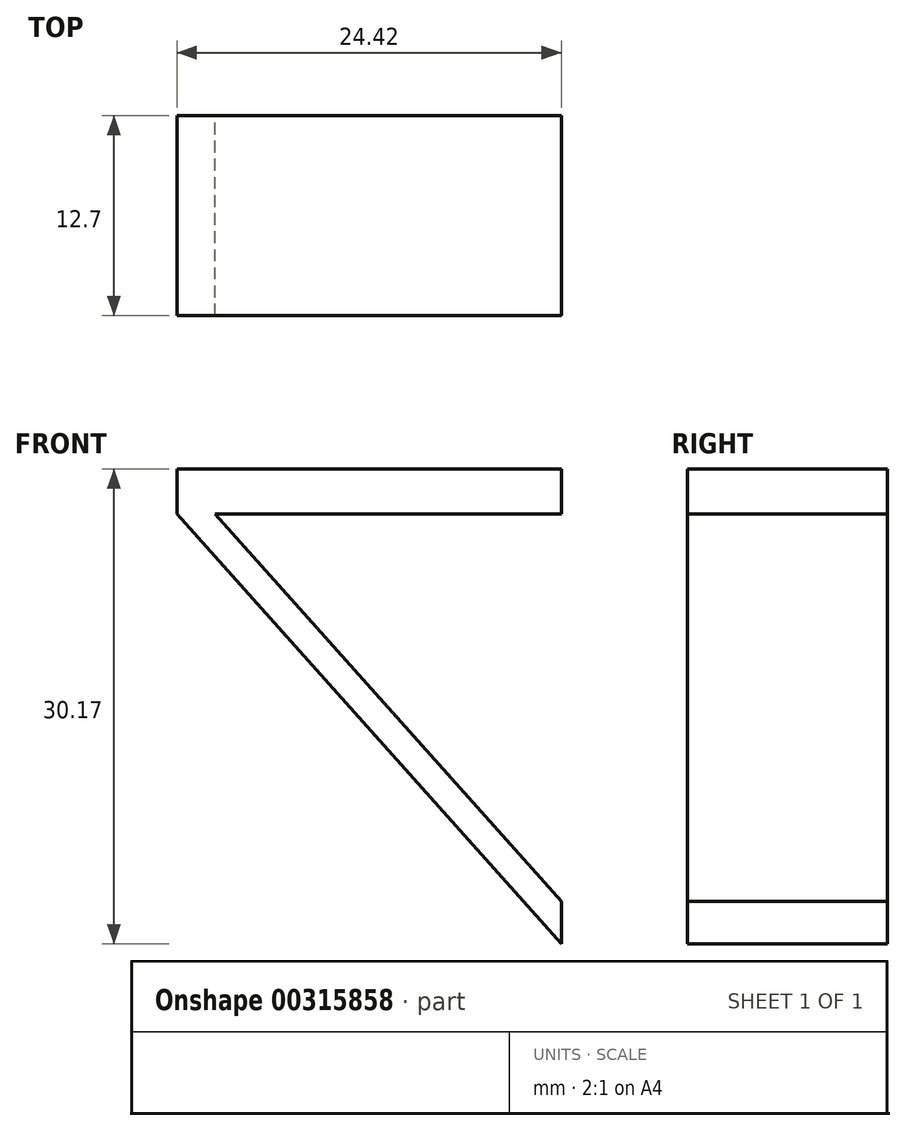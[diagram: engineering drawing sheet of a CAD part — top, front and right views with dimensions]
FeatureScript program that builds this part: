
annotation { "Feature Type Name" : "Feature", "Feature Type Description" : "" }
export const myFeature = defineFeature(function(context is Context, id is Id, definition is map)
    precondition{}
    {
        {
            var Q0;
            Q0=qCreatedBy(makeId("Front.planeOp"),FACE);
            var sketch = newSketch(context, id + "F0", { "sketchPlane" : qUnion([Q0])});
            skLineSegment(sketch, "E0", {"start": v(0, 0) * mm, "end": v(-21.99, 0) * mm});
            skLineSegment(sketch, "E1", {"start": v(-21.99, 0) * mm, "end": v(-21.99, 2.86) * mm});
            skLineSegment(sketch, "E2", {"start": v(0, 0) * mm, "end": v(0, 2.86) * mm});
            skLineSegment(sketch, "E3", {"start": v(0, 2.86) * mm, "end": v(0, 0) * mm});
            skLineSegment(sketch, "E4", {"start": v(-21.99, 2.86) * mm, "end": v(0, 2.86) * mm});
            skLineSegment(sketch, "E5", {"start": v(-21.99, 0) * mm, "end": v(0, -24.6) * mm});
            skLineSegment(sketch, "E6", {"start": v(0, -24.6) * mm, "end": v(0, -27.3) * mm});
            skLineSegment(sketch, "E7", {"start": v(0, -27.3) * mm, "end": v(-21.99, -2.72) * mm});
            skLineSegment(sketch, "E8", {"start": v(-21.99, -2.72) * mm, "end": v(-24.42, 0) * mm});
            skLineSegment(sketch, "E9", {"start": v(-24.42, 0) * mm, "end": v(-24.42, 2.86) * mm});
            skLineSegment(sketch, "E10", {"start": v(-24.42, 2.86) * mm, "end": v(-21.99, 2.86) * mm});
            skSolve(sketch);
        }
        {
            var Q0;
            Q0 = qSketchRegion(id + "F0", true);
            extrude(context, id + "F1", {"entities" : qUnion([Q0]), "depth" : 12.7 * mm});
        }
    });
